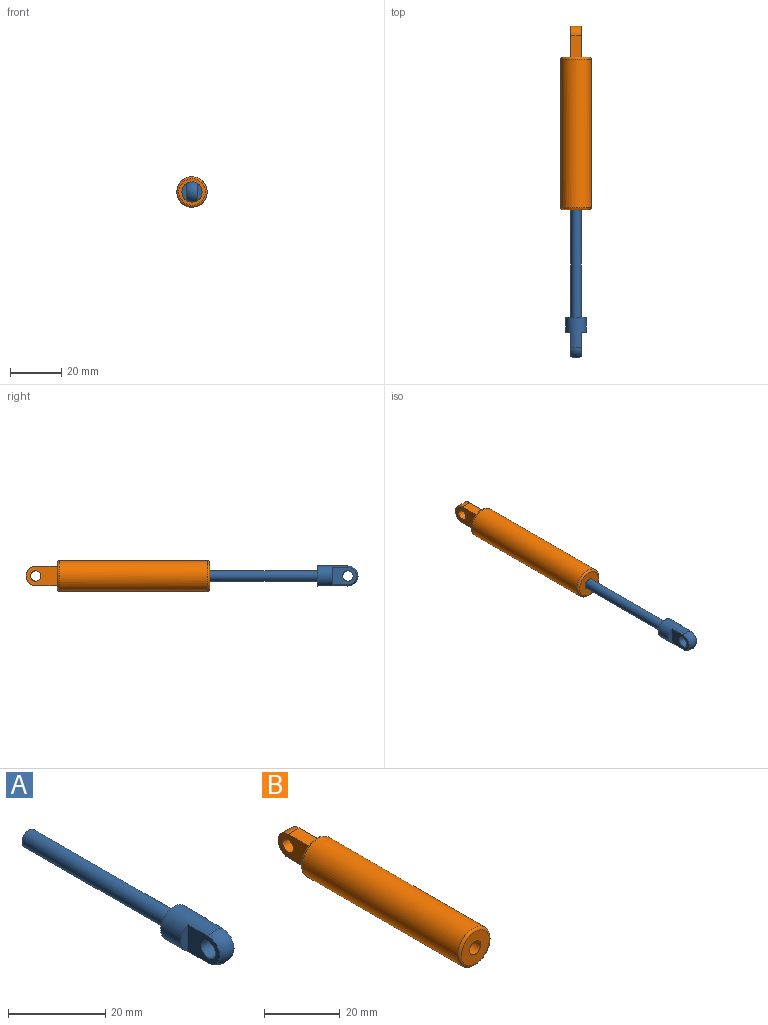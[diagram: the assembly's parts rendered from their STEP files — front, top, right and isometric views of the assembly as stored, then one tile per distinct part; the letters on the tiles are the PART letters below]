
ASSEMBLY  parts=2 mates=1
PART A: 10 faces, bbox 7.9x58.1x7.9 mm
  f0: cylinder r=3.94mm len=11.94mm, axis (0,1,0), area 196.6mm2, adj f1,f4,f5,f6,f7,f8
  f1: sphere r=3.94mm, area 50.3mm2, adj f0,f5,f8
  f2: plane 4.06x4.06mm, normal (0,1,0), area 13mm2, adj f3
  f3: cylinder r=2.03mm len=42.22mm, axis (0,1,0), area 539mm2, adj f2,f4
  f4: plane 7.87x7.87mm, normal (0,1,0), area 35.7mm2, adj f0,f3
  f5: plane 9.47x6.74mm, normal (1,0,0), area 46mm2, adj f0,f1,f6,f9
  f6: plane 6.74x1.91mm, normal (0,-1,0), area 9.1mm2, adj f0,f5
  f7: plane 6.74x1.91mm, normal (0,-1,0), area 9.1mm2, adj f0,f8
  f8: plane 9.47x6.74mm, normal (-1,0,0), area 46mm2, adj f0,f1,f7,f9
  f9: cylinder r=2.03mm len=4.06mm, axis (1,0,0), area 51.9mm2, adj f5,f8
PART B: 13 faces, bbox 12.9x71.8x12.9 mm
  f0: plane 10.38x10.38mm, normal (0,1,0), area 53.7mm2, adj f5,f7,f8,f9,f11
  f1: cylinder r=5.97mm len=58.08mm, axis (0,-1,0), area 2178.4mm2, adj f5,f6
  f2: plane 10.38x10.38mm, normal (0,-1,0), area 71.1mm2, adj f3,f6
  f3: cylinder r=2.08mm len=42.22mm, axis (0,-1,0), area 552.4mm2, adj f2,f4
  f4: plane 4.17x4.17mm, normal (0,-1,0), area 13.6mm2, adj f3
  f5: torus R=5.19mm, axis (0,-1,0), area 43.6mm2, adj f0,f1
  f6: torus R=5.19mm, axis (0,1,0), area 43.6mm2, adj f1,f2
  f7: plane 12.19x7.62mm, normal (1,0,0), area 73.7mm2, adj f0,f9,f10,f11,f12
  f8: plane 12.19x7.62mm, normal (-1,0,0), area 73.7mm2, adj f0,f9,f10,f11,f12
  f9: plane 8.38x4.06mm, normal (0,0,-1), area 34.1mm2, adj f0,f7,f8,f10
  f10: cylinder r=3.81mm len=7.62mm, axis (-1,0,0), area 48.6mm2, adj f7,f8,f9,f11
  f11: plane 8.38x4.06mm, normal (0,0,1), area 34.1mm2, adj f0,f7,f8,f10
  f12: cylinder r=2.03mm len=4.06mm, axis (-1,0,0), area 51.9mm2, adj f7,f8
PLACE A t=(11.09,-19.05,14.44)mm
PLACE B t=(11.09,-6.86,14.44)mm
MATE slider A.f3 <-> B.f1  axis (0,1,0) through (11.09,-19.89,14.44)mm
